# Revit family: Furniture-Mirror-KOHLER-FAMILY_CARE-K-25242T_1
name_source: partatom
category: Specialty Equipment
units: mm (PartAtom-declared; Revit-internal decimal feet)

## family parameters
Cut with Voids When Loaded = No
Host = Face
OmniClass Number = 23.21.37.13.15
OmniClass Title = Mirrors
Part Type = Normal
Room Calculation Point = No
Round Connector Dimension = Use Diameter
Shared = No

## types (1)
- NA-Mild Steel
    ADA Compliant = No
    Assembly Code = E20
    Date Modified = 07/26/2022
    Default Elevation = 48"
    Description = Children's Mirror 1000mm
    Finish = KOHLER-Metal-NA-Mild_Silver
    Height = 10 9/16"
    Length = 38 1/2"
    Manufacturer = Kohler Co.
    Master Format 2014 = 06 41 93
    Master Format 2014 Name = Cabinet and Drawer Hardware
    Material = Aluminium
    Model = K-25242T-NA
    Product Documentation Link = https://files.kohler.com.cn
    Product Name = Family Care
    Product Page URL = https://www.kohler.com.cn
    Type = 1
    URL = http://www.kohler.com.cn
    WaterSense Certified = No
    Width = 3/8"

## geometry (parser evidence)
native form markers: Sweep x6
no freeform markers — native parametric forms only
